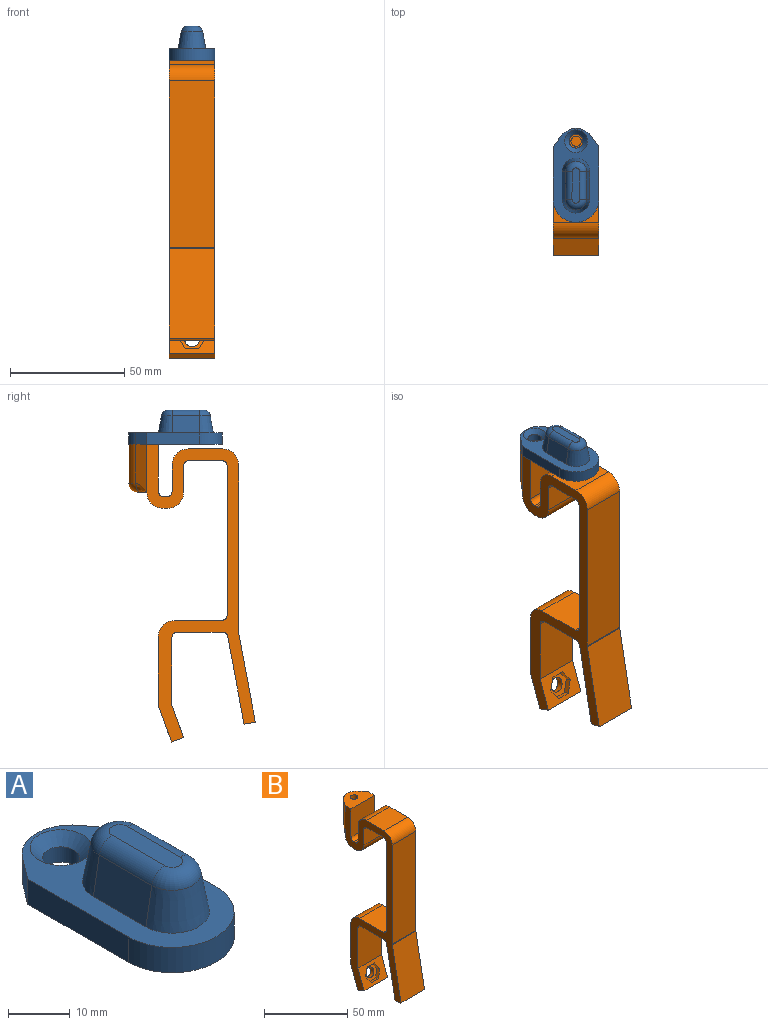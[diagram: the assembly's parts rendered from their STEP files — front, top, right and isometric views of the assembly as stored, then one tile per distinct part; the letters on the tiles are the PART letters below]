
ASSEMBLY  parts=2 mates=1
PART A: 21 faces, bbox 20x41x15 mm
  f0: plane 41x20mm, normal (0,0,1), area 388.8mm2, adj f1,f2,f3,f4,f5,f6,f9,f10
  f1: plane 23x5mm, normal (-1,0,0), area 115mm2, adj f0,f2,f6,f8
  f2: cylinder r=10mm len=20mm, axis (0,0,-1), area 157.1mm2, adj f0,f1,f3,f8
  f3: plane 23x5mm, normal (1,0,0), area 115mm2, adj f0,f2,f4,f8
  f4: plane 5x4.8mm, normal (0.8,0.6,0), area 30mm2, adj f0,f3,f5,f8
  f5: cylinder r=8mm len=12.8mm, axis (0,0,-1), area 74.2mm2, adj f0,f4,f6,f8
  f6: plane 5x4.8mm, normal (-0.8,0.6,0), area 30mm2, adj f0,f1,f5,f8
  f7: cylinder r=3mm len=6mm, axis (0,0,-1), area 56.5mm2, adj f8,f9
  f8: plane 41x20mm, normal (0,0,-1), area 643.3mm2, adj f1,f2,f3,f4,f5,f6,f7,f19
  f9: cone r=3mm half-angle=45deg, axis (0,0,1), area 71.1mm2, adj f0,f7
  f10: cone r=6mm half-angle=10deg, axis (0,0,-1), area 128mm2, adj f0,f11,f13,f17
  f11: plane 12x7.52mm, normal (-0.98,0,0.17), area 91.6mm2, adj f0,f10,f12,f15
  f12: cone r=6mm half-angle=10deg, axis (0,0,-1), area 128mm2, adj f0,f11,f13,f16
  f13: plane 12x7.52mm, normal (0.98,0,0.17), area 91.6mm2, adj f0,f10,f12,f18
  f14: plane 15.44x3.44mm, normal (0,0,1), area 50.6mm2, adj f15,f16,f17,f18
  f15: cylinder r=3mm len=12mm, axis (0,1,0), area 50.3mm2, adj f11,f14,f16,f17
  f16: torus R=1.72mm, axis (0,0,1), area 46mm2, adj f12,f14,f15,f18
  f17: torus R=1.72mm, axis (0,0,1), area 46mm2, adj f10,f14,f15,f18
  f18: cylinder r=3mm len=12mm, axis (0,1,0), area 50.3mm2, adj f13,f14,f16,f17
  f19: cylinder r=4.1mm len=8.2mm, axis (0,0,-1), area 95.3mm2, adj f8,f20
  f20: plane 8.2x8.2mm, normal (0,0,-1), area 52.8mm2, adj f19
PART B: 54 faces, bbox 20x56x130 mm
  f0: plane 20x15mm, normal (0,0,1), area 300mm2, adj f20,f21,f30,f34
  f1: plane 72.77x20mm, normal (0,-1,0), area 1455.4mm2, adj f20,f21,f22,f30
  f2: plane 39.09x20mm, normal (0,-0.98,0.18), area 795.4mm2, adj f3,f20,f21,f22
  f3: plane 20x4.91mm, normal (0,-0.18,-0.98), area 100mm2, adj f2,f4,f20,f21
  f4: plane 38.2x20mm, normal (0,0.98,-0.18), area 777.2mm2, adj f3,f20,f21,f23
  f5: plane 20x19.42mm, normal (0,0,-1), area 388.5mm2, adj f20,f21,f23,f24
  f6: plane 29.5x20mm, normal (0,-1,0), area 590mm2, adj f7,f20,f21,f24
  f7: plane 20x14.1mm, normal (0,-0.94,0.34), area 206.3mm2, adj f6,f8,f20,f21,f45,f46,f47,f48
  f8: plane 20x5.3mm, normal (0,-0.34,-0.94), area 112.8mm2, adj f7,f9,f20,f21
  f9: plane 20x16.02mm, normal (0,0.94,-0.34), area 307.9mm2, adj f8,f10,f20,f21,f51
  f10: plane 30x20mm, normal (0,1,0), area 600mm2, adj f9,f20,f21,f31
  f11: plane 20.59x20mm, normal (0,0,1), area 411.7mm2, adj f20,f21,f25,f31
  f12: plane 65x20mm, normal (0,1,0), area 1300mm2, adj f20,f21,f25,f26
  f13: plane 20x14mm, normal (0,0,-1), area 227.2mm2, adj f20,f21,f26,f27,f53
  f14: plane 20x11.5mm, normal (0,-1,0), area 230mm2, adj f20,f21,f27,f32
  f15: plane 20x2mm, normal (0,0,-1), area 40mm2, adj f20,f21,f32,f33
  f16: plane 20x13mm, normal (0,0,1), area 191.4mm2, adj f17,f20,f21,f35,f36,f37,f42
  f17: plane 20.5x20mm, normal (0,-1,0), area 410mm2, adj f16,f20,f21,f28
  f18: plane 20x1mm, normal (0,0,1), area 20mm2, adj f20,f21,f28,f29
  f19: plane 20x11.5mm, normal (0,1,0), area 230mm2, adj f20,f21,f29,f34
  f20: plane 130.02x47.36mm, normal (1,0,0), area 1386.5mm2, adj f0,f1,f2,f3,f4,f5,f6,f7
  f21: plane 130.02x47.36mm, normal (-1,0,0), area 1386.5mm2, adj f0,f1,f2,f3,f4,f5,f6,f7
  f22: cylinder r=2.5mm len=20mm, axis (-1,0,0), area 9.3mm2, adj f1,f2,f20,f21
  f23: cylinder r=2.5mm len=20mm, axis (1,0,0), area 69.3mm2, adj f4,f5,f20,f21
  f24: cylinder r=2.5mm len=20mm, axis (1,0,0), area 78.5mm2, adj f5,f6,f20,f21
  f25: cylinder r=2.5mm len=20mm, axis (-1,0,0), area 78.5mm2, adj f11,f12,f20,f21
  f26: cylinder r=2.5mm len=20mm, axis (1,0,0), area 78.5mm2, adj f12,f13,f20,f21
  f27: cylinder r=2.5mm len=20mm, axis (1,0,0), area 78.5mm2, adj f13,f14,f20,f21
  f28: cylinder r=2.5mm len=20mm, axis (1,0,0), area 78.5mm2, adj f17,f18,f20,f21
  f29: cylinder r=2.5mm len=20mm, axis (1,0,0), area 78.5mm2, adj f18,f19,f20,f21
  f30: cylinder r=7mm len=20mm, axis (-1,0,0), area 219.9mm2, adj f0,f1,f20,f21
  f31: cylinder r=7mm len=20mm, axis (-1,0,0), area 219.9mm2, adj f10,f11,f20,f21
  f32: cylinder r=7mm len=20mm, axis (-1,0,0), area 219.9mm2, adj f14,f15,f20,f21
  f33: cylinder r=7mm len=20mm, axis (-1,0,0), area 219.9mm2, adj f15,f20,f21,f38
  f34: cylinder r=7mm len=20mm, axis (-1,0,0), area 219.9mm2, adj f0,f19,f20,f21
  f35: cylinder r=8mm len=17mm, axis (0,0,1), area 252.2mm2, adj f16,f36,f37,f40
  f36: plane 21x4.8mm, normal (-0.8,0.6,0), area 111mm2, adj f16,f21,f35,f41
  f37: plane 21x4.8mm, normal (0.8,0.6,0), area 111mm2, adj f16,f20,f35,f39
  f38: plane 20x4mm, normal (0,0,-1), area 32.8mm2, adj f33,f39,f40,f41
  f39: bspline ~6.8x4.8mm, area 23.9mm2, adj f37,f38,f40
  f40: torus R=4mm, axis (0,0,1), area 76.3mm2, adj f35,f38,f39,f41
  f41: bspline ~6.8x4.8mm, area 23.9mm2, adj f36,f38,f40
  f42: cylinder r=2.25mm len=18mm, axis (0,0,1), area 254.5mm2, adj f16,f43
  f43: plane 4.5x4.5mm, normal (0,0,1), area 15.9mm2, adj f42
  f44: plane 12.01x9.77mm, normal (0,-0.94,0.34), area 60.5mm2, adj f45,f46,f47,f48,f49,f50,f51
  f45: plane 6x2.48mm, normal (0,0.34,0.94), area 15.8mm2, adj f7,f44,f46,f50
  f46: plane 5.79x4.26mm, normal (-0.87,0.17,0.47), area 15.8mm2, adj f7,f44,f45,f47
  f47: plane 5.79x4.26mm, normal (-0.87,-0.17,-0.47), area 15.8mm2, adj f7,f44,f46,f48
  f48: plane 6x2.48mm, normal (0,-0.34,-0.94), area 15.8mm2, adj f7,f44,f47,f49
  f49: plane 5.79x4.26mm, normal (0.87,-0.17,-0.47), area 15.8mm2, adj f7,f44,f48,f50
  f50: plane 5.79x4.26mm, normal (0.87,0.17,0.47), area 15.8mm2, adj f7,f44,f45,f49
  f51: cylinder r=3.25mm len=7.13mm, axis (0,-0.94,0.34), area 61.3mm2, adj f9,f44
  f52: plane 8.2x8.2mm, normal (0,0,-1), area 52.8mm2, adj f53
  f53: cylinder r=4.1mm len=8.2mm, axis (0,0,-1), area 103mm2, adj f13,f52
PLACE A rot(axis=(0,0,-1),0.2deg) t=(-0.13,0,0)mm
PLACE B at identity fixed
MATE revolute A.f7 <-> B.f42  axis (0,0,-1) through (0,42.4,82)mm
